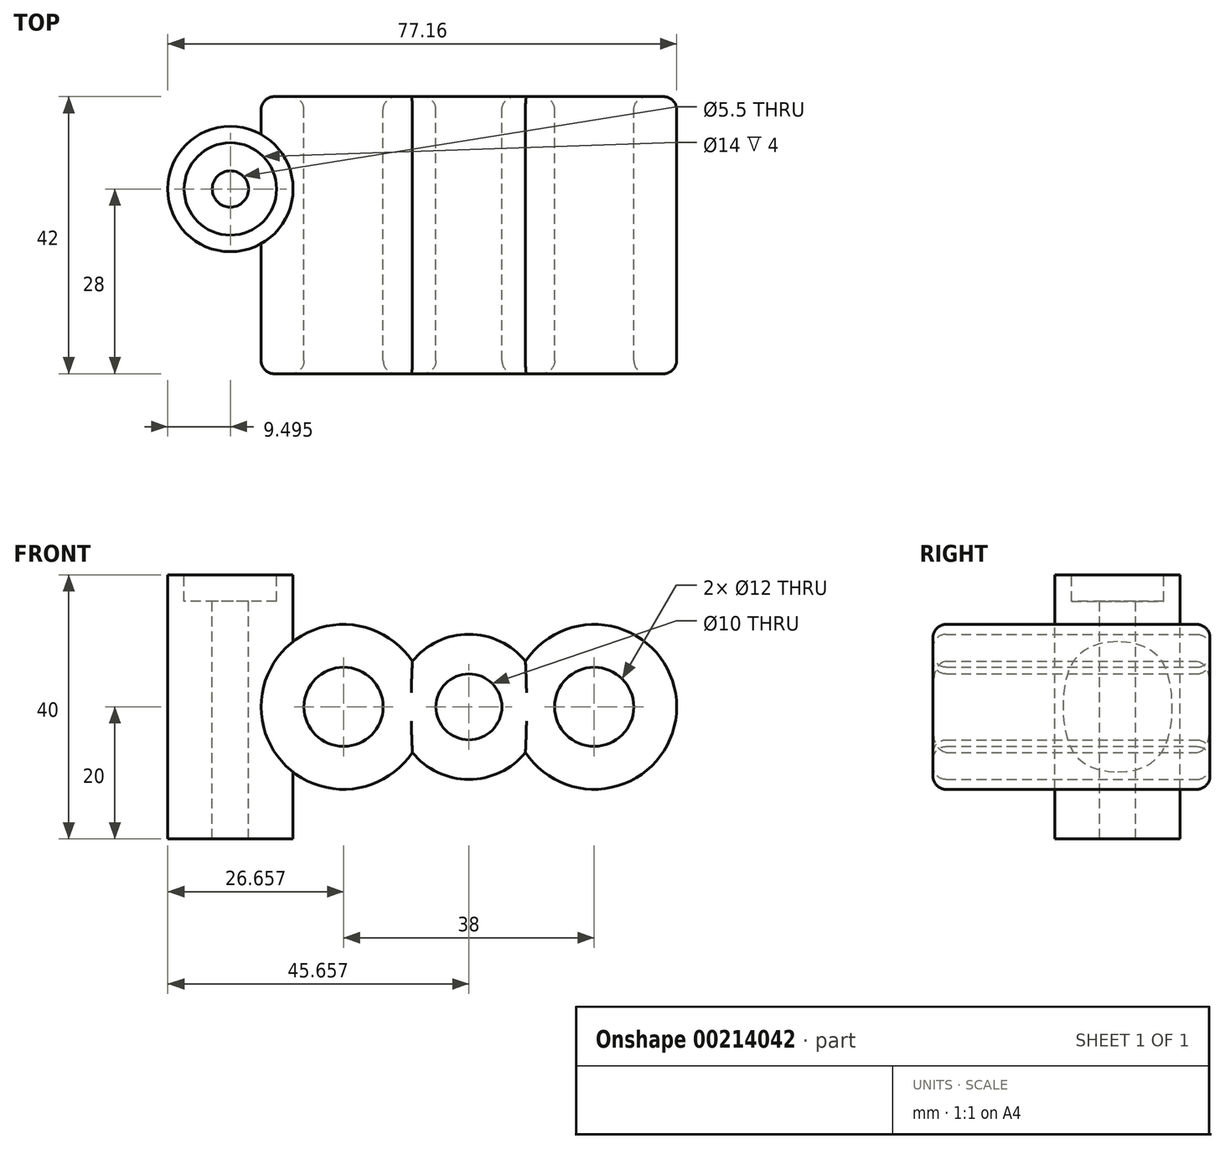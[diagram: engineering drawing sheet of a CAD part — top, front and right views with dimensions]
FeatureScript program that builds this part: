
annotation { "Feature Type Name" : "Feature", "Feature Type Description" : "" }
export const myFeature = defineFeature(function(context is Context, id is Id, definition is map)
    precondition{}
    {
        {
            var Q0;
            Q0=qCreatedBy(makeId("Front.planeOp"),FACE);
            var sketch = newSketch(context, id + "F0", { "sketchPlane" : qUnion([Q0])});
            skCircle(sketch, "E0", {"center": v(-33.37, 0) * mm, "radius": 6 * mm});
            skCircle(sketch, "E1", {"center": v(-14.37, 0) * mm, "radius": 5 * mm});
            skCircle(sketch, "E2", {"center": v(4.63, 0) * mm, "radius": 6 * mm});
            skCircle(sketch, "E3", {"center": v(4.63, 0) * mm, "radius": 12.5 * mm});
            skCircle(sketch, "E4", {"center": v(-33.37, 0) * mm, "radius": 12.5 * mm});
            skCircle(sketch, "E5", {"center": v(-14.37, 0) * mm, "radius": 11 * mm});
            skSolve(sketch);
        }
        {
            var Q0;
            Q0 = qSketchRegion(id + "F0", true);
            extrude(context, id + "F1", {"entities" : qUnion([Q0]), "depth" : 42 * mm});
        }
        {
            var Q0;
            Q0=makeQuery(id+"F1.opExtrude","CAP_FACE",FACE,{"disambiguationData":[OSD([sQuery(id+"F0.wireOp",EDGE,"E0"),sQuery(id+"F0.wireOp",EDGE,"E1"),sQuery(id+"F0.wireOp",EDGE,"E2"),sQuery(id+"F0.wireOp",EDGE,"E3"),sQuery(id+"F0.wireOp",EDGE,"E4"),sQuery(id+"F0.wireOp",EDGE,"E5")])],"isStart":false});
            var Q1;
            Q1=makeQuery(id+"F1.opExtrude","CAP_FACE",FACE,{"disambiguationData":[OSD([sQuery(id+"F0.wireOp",EDGE,"E0"),sQuery(id+"F0.wireOp",EDGE,"E1"),sQuery(id+"F0.wireOp",EDGE,"E2"),sQuery(id+"F0.wireOp",EDGE,"E3"),sQuery(id+"F0.wireOp",EDGE,"E4"),sQuery(id+"F0.wireOp",EDGE,"E5")])],"isStart":true});
            fillet(context, id + "F2", {"entities" : qUnion([Q0, Q1]), "radius" : 2 * mm, "tangentPropagation" : true, "allowEdgeOverflow" : false});
        }
        {
            var Q0;
            Q0=qCreatedBy(makeId("Top.planeOp"),FACE);
            var sketch = newSketch(context, id + "F3", { "sketchPlane" : qUnion([Q0])});
            skCircle(sketch, "E6", {"center": v(-50.53, -14) * mm, "radius": 9.5 * mm});
            skSolve(sketch);
        }
        {
            var Q0;
            Q0=makeQuery(id+"F3.imprint","IMPRINT",FACE,{"disambiguationData":[TD([[makeQuery(id+"F3.imprint","IMPRINT",EDGE,{"derivedFrom":sQuery(id+"F3.wireOp",EDGE,"E6")}),1.0]])]});
            extrude(context, id + "F4", {"entities" : qUnion([Q0]), "operationType" : NewBodyOperationType.ADD, "oppositeDirection" : true, "depth" : 20 * mm, "hasSecondDirection" : true, "secondDirectionOppositeDirection" : false, "secondDirectionDepth" : 20 * mm});
        }
        {
            var Q0;
            Q0=makeQuery(id+"F4.opExtrude","CAP_FACE",FACE,{"disambiguationData":[OSD([sQuery(id+"F3.wireOp",EDGE,"E6")])],"isStart":true});
            var sketch = newSketch(context, id + "F5", { "sketchPlane" : qUnion([Q0])});
            skPoint(sketch, "E7", {"position": v(-50.53, -14) * mm});
            skCircle(sketch, "E8", {"center": v(-50.53, -14) * mm, "radius": 7 * mm});
            skSolve(sketch);
        }
        {
            var Q0;
            Q0=sQuery(id+"F5.wireOp",VERTEX,"E7");
            var Q1;
            Q1=makeQuery(id+"F1.opExtrude","SWEPT_BODY",BODY,{"disambiguationData":[OSD([sQuery(id+"F0.wireOp",EDGE,"E0"),sQuery(id+"F0.wireOp",EDGE,"E1"),sQuery(id+"F0.wireOp",EDGE,"E2"),sQuery(id+"F0.wireOp",EDGE,"E3"),sQuery(id+"F0.wireOp",EDGE,"E4"),sQuery(id+"F0.wireOp",EDGE,"E5")])]});
            hole(context, id + "F6", {"style" : HoleStyle.SIMPLE, "endStyle" : HoleEndStyle.THROUGH, "standardTappedOrClearance" : lookupTablePath({ "standard" : "ISO", "fit" : "Normal", "size" : "M5", "type" : "Clearance" }), "standardBlindInLast" : lookupTablePath({ "fit" : "Standard", "standard" : "ISO", "size" : "M5", "type" : "Clearance" }), "holeDiameter" : 5.5 * mm, "locations" : qUnion([Q0]), "scope" : qUnion([Q1]), "isTappedThrough" : true});
        }
        {
            var Q0;
            Q0 = qSketchRegion(id + "F5", true);
            var Q1;
            Q1=makeQuery(id+"F4.opExtrude","CAP_FACE",FACE,{"disambiguationData":[OSD([sQuery(id+"F3.wireOp",EDGE,"E6")])],"isStart":false});
            extrude(context, id + "F7", {"entities" : qUnion([Q0, Q1]), "operationType" : NewBodyOperationType.REMOVE, "oppositeDirection" : true, "depth" : 4 * mm});
        }
    });
